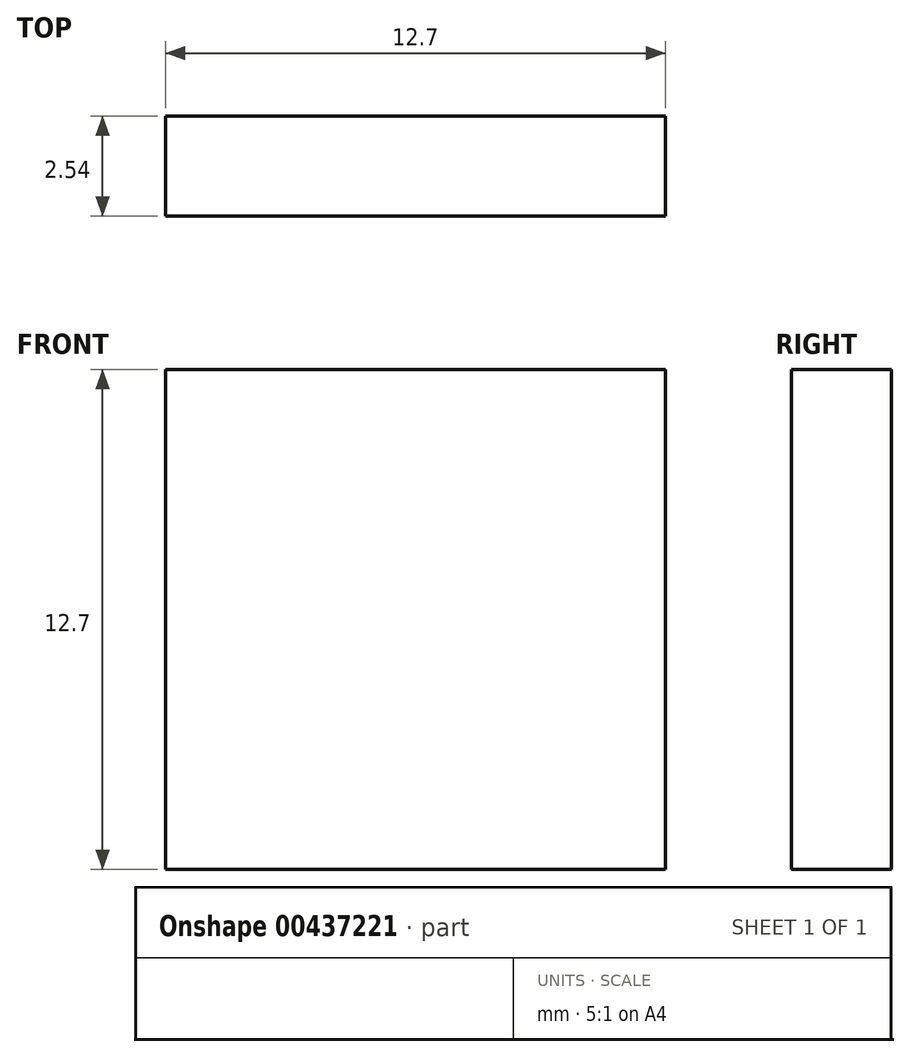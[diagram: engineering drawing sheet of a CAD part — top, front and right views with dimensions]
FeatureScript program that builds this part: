
annotation { "Feature Type Name" : "Feature", "Feature Type Description" : "" }
export const myFeature = defineFeature(function(context is Context, id is Id, definition is map)
    precondition{}
    {
        {
            var Q0;
            Q0=qCreatedBy(makeId("Front.planeOp"),FACE);
            var sketch = newSketch(context, id + "F0", { "sketchPlane" : qUnion([Q0])});
            skLineSegment(sketch, "E0.bottom", {"start": v(-5.4, 12.85) * mm, "end": v(7.3, 12.85) * mm});
            skLineSegment(sketch, "E0.top", {"start": v(-5.4, 0.15) * mm, "end": v(7.3, 0.15) * mm});
            skLineSegment(sketch, "E0.left", {"start": v(-5.4, 12.85) * mm, "end": v(-5.4, 0.15) * mm});
            skLineSegment(sketch, "E0.right", {"start": v(7.3, 12.85) * mm, "end": v(7.3, 0.15) * mm});
            skSolve(sketch);
        }
        {
            var Q0;
            Q0 = qSketchRegion(id + "F0", true);
            extrude(context, id + "F1", {"entities" : qUnion([Q0]), "depth" : 2.54 * mm});
        }
    });
